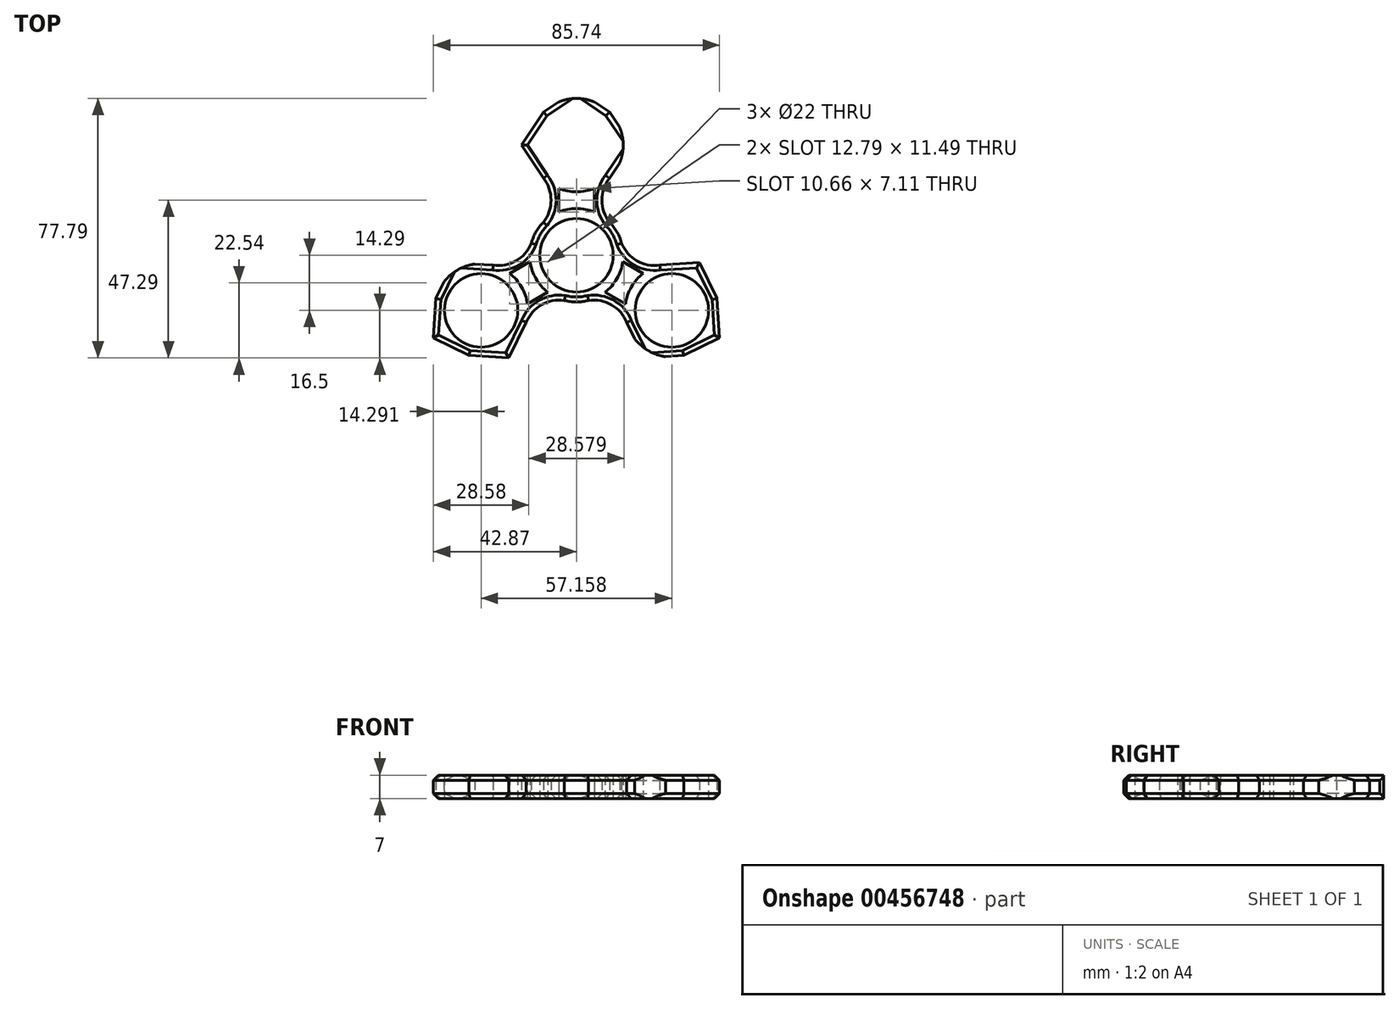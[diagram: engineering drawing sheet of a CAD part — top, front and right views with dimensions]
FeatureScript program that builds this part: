
annotation { "Feature Type Name" : "Feature", "Feature Type Description" : "" }
export const myFeature = defineFeature(function(context is Context, id is Id, definition is map)
    precondition{}
    {
        {
            var Q0;
            Q0=qCreatedBy(makeId("Top.planeOp"),FACE);
            var sketch = newSketch(context, id + "F0", { "sketchPlane" : qUnion([Q0])});
            skCircle(sketch, "E0", {"center": v(0, 0) * mm, "radius": 11 * mm});
            skArc(sketch, "E1.0", {"start": v(-9.9, 9.9) * mm, "mid": v(0, -14) * mm, "end": v(9.9, 9.9) * mm});
            skCircle(sketch, "E2.MirrorC", {"center": v(0, 33) * mm, "radius": 11 * mm});
            skArc(sketch, "E3.MirrorC", {"start": v(5.33, 20.06) * mm, "mid": v(0, 19) * mm, "end": v(-5.33, 20.06) * mm});
            skLineSegment(sketch, "E4.MirrorCS", {"start": v(0, 33) * mm, "end": v(0, 16.5) * mm});
            skLineSegment(sketch, "E5.MirrorCS", {"start": v(-9.9, 23.1) * mm, "end": v(0, 16.5) * mm});
            skLineSegment(sketch, "E6.MirrorCS", {"start": v(0, 16.5) * mm, "end": v(9.9, 23.1) * mm});
            skArc(sketch, "E7.trimOffspring", {"start": v(5.33, 12.94) * mm, "mid": v(0, 14) * mm, "end": v(-5.33, 12.94) * mm});
            skLineSegment(sketch, "E8", {"start": v(5.33, 20.06) * mm, "end": v(5.33, 12.94) * mm});
            skLineSegment(sketch, "E9", {"start": v(-5.33, 12.94) * mm, "end": v(-5.33, 20.06) * mm});
            skLineSegment(sketch, "E10", {"start": v(0, 33) * mm, "end": v(7.48, 33) * mm});
            skLineSegment(sketch, "E11.MirrorCS", {"start": v(0, 49.5) * mm, "end": v(9.9, 42.9) * mm});
            skLineSegment(sketch, "E12.MirrorCS", {"start": v(-9.9, 42.9) * mm, "end": v(0, 49.5) * mm});
            skArc(sketch, "E13.trimOffspring", {"start": v(-5.33, 45.94) * mm, "mid": v(0, 47) * mm, "end": v(5.33, 45.94) * mm});
            skArc(sketch, "E14.trimOffspring", {"start": v(12.94, 38.33) * mm, "mid": v(14, 33) * mm, "end": v(12.94, 27.67) * mm});
            skPoint(sketch, "E15", {"position": v(7.62, 16.5) * mm});
            skArc(sketch, "E16", {"start": v(9.9, 23.1) * mm, "mid": v(7.62, 16.5) * mm, "end": v(9.9, 9.9) * mm});
            skPoint(sketch, "E17.start.orphan", {"position": v(9.9, 16.5) * mm});
            skArc(sketch, "E18.MirrorCS", {"start": v(-9.9, 23.1) * mm, "mid": v(-7.62, 16.5) * mm, "end": v(-9.9, 9.9) * mm});
            skPoint(sketch, "E19.start.orphan", {"position": v(5.33, 16.5) * mm});
            skLineSegment(sketch, "E20.1.0", {"start": v(16.5, 33) * mm, "end": v(9.9, 23.1) * mm});
            skLineSegment(sketch, "E20.1.1", {"start": v(9.9, 42.9) * mm, "end": v(16.5, 33) * mm});
            skLineSegment(sketch, "E20.3.0", {"start": v(-16.5, 33) * mm, "end": v(-9.9, 42.9) * mm});
            skLineSegment(sketch, "E20.3.1", {"start": v(-9.9, 23.1) * mm, "end": v(-16.5, 33) * mm});
            skLineSegment(sketch, "E20.anchor1", {"start": v(0, 33) * mm, "end": v(0, 49.5) * mm, "construction": true});
            skLineSegment(sketch, "E20.anchor2", {"start": v(0, 33) * mm, "end": v(-16.5, 33) * mm, "construction": true});
            skLineSegment(sketch, "E21.1.0", {"start": v(-42.87, -24.75) * mm, "end": v(-42.1, -12.88) * mm});
            skLineSegment(sketch, "E21.1.1", {"start": v(-32.2, -30.02) * mm, "end": v(-42.87, -24.75) * mm});
            skArc(sketch, "E21.1.2", {"start": v(-37.12, -27.6) * mm, "mid": v(-40.7, -23.5) * mm, "end": v(-42.46, -18.35) * mm});
            skLineSegment(sketch, "E21.1.3", {"start": v(-20.33, -30.79) * mm, "end": v(-32.2, -30.02) * mm});
            skCircle(sketch, "E21.1.4", {"center": v(-28.58, -16.5) * mm, "radius": 11 * mm});
            skLineSegment(sketch, "E21.1.5", {"start": v(-15.06, -20.12) * mm, "end": v(-20.33, -30.79) * mm});
            skLineSegment(sketch, "E21.1.6", {"start": v(-15.06, -20.12) * mm, "end": v(-14.29, -8.25) * mm});
            skArc(sketch, "E21.1.7", {"start": v(-20.03, -5.4) * mm, "mid": v(-16.45, -9.5) * mm, "end": v(-14.7, -14.65) * mm});
            skLineSegment(sketch, "E21.1.8", {"start": v(-14.29, -8.25) * mm, "end": v(-24.96, -2.98) * mm});
            skArc(sketch, "E21.1.9", {"start": v(-39.67, -7.96) * mm, "mid": v(-35.58, -4.38) * mm, "end": v(-30.43, -2.62) * mm});
            skLineSegment(sketch, "E21.1.10", {"start": v(-36.83, -2.21) * mm, "end": v(-24.96, -2.98) * mm});
            skLineSegment(sketch, "E21.1.11", {"start": v(-42.1, -12.88) * mm, "end": v(-36.83, -2.21) * mm});
            skArc(sketch, "E21.1.12", {"start": v(-24.96, -2.98) * mm, "mid": v(-18.1, -1.65) * mm, "end": v(-13.52, 3.62) * mm});
            skLineSegment(sketch, "E21.1.13", {"start": v(-20.03, -5.4) * mm, "end": v(-13.88, -1.85) * mm});
            skLineSegment(sketch, "E21.1.14", {"start": v(-8.54, -11.1) * mm, "end": v(-14.7, -14.65) * mm});
            skArc(sketch, "E21.1.15", {"start": v(-15.06, -20.12) * mm, "mid": v(-10.48, -14.85) * mm, "end": v(-3.62, -13.52) * mm});
            skLineSegment(sketch, "E21.2.0", {"start": v(42.87, -24.75) * mm, "end": v(32.2, -30.02) * mm});
            skLineSegment(sketch, "E21.2.1", {"start": v(42.1, -12.88) * mm, "end": v(42.87, -24.75) * mm});
            skArc(sketch, "E21.2.2", {"start": v(42.46, -18.35) * mm, "mid": v(40.7, -23.5) * mm, "end": v(37.12, -27.6) * mm});
            skLineSegment(sketch, "E21.2.3", {"start": v(36.83, -2.21) * mm, "end": v(42.1, -12.88) * mm});
            skCircle(sketch, "E21.2.4", {"center": v(28.58, -16.5) * mm, "radius": 11 * mm});
            skLineSegment(sketch, "E21.2.5", {"start": v(24.96, -2.98) * mm, "end": v(36.83, -2.21) * mm});
            skLineSegment(sketch, "E21.2.6", {"start": v(24.96, -2.98) * mm, "end": v(14.29, -8.25) * mm});
            skArc(sketch, "E21.2.7", {"start": v(14.7, -14.65) * mm, "mid": v(16.45, -9.5) * mm, "end": v(20.03, -5.4) * mm});
            skLineSegment(sketch, "E21.2.8", {"start": v(14.29, -8.25) * mm, "end": v(15.06, -20.12) * mm});
            skArc(sketch, "E21.2.9", {"start": v(26.72, -30.38) * mm, "mid": v(21.58, -28.62) * mm, "end": v(17.49, -25.04) * mm});
            skLineSegment(sketch, "E21.2.10", {"start": v(20.33, -30.79) * mm, "end": v(15.06, -20.12) * mm});
            skLineSegment(sketch, "E21.2.11", {"start": v(32.2, -30.02) * mm, "end": v(20.33, -30.79) * mm});
            skArc(sketch, "E21.2.12", {"start": v(15.06, -20.12) * mm, "mid": v(10.48, -14.85) * mm, "end": v(3.62, -13.52) * mm});
            skLineSegment(sketch, "E21.2.13", {"start": v(14.7, -14.65) * mm, "end": v(8.54, -11.1) * mm});
            skLineSegment(sketch, "E21.2.14", {"start": v(13.88, -1.85) * mm, "end": v(20.03, -5.4) * mm});
            skArc(sketch, "E21.2.15", {"start": v(24.96, -2.98) * mm, "mid": v(18.1, -1.65) * mm, "end": v(13.52, 3.62) * mm});
            skSolve(sketch);
        }
        {
            var Q0;
            Q0=makeQuery(id+"F0.imprint","IMPRINT",FACE,{"disambiguationData":[TD([[makeQuery(id+"F0.imprint","IMPRINT",EDGE,{"derivedFrom":sQuery(id+"F0.wireOp",EDGE,"E0")}),-1.0]])]});
            var Q1;
            Q1=makeQuery(id+"F0.imprint","IMPRINT",FACE,{"disambiguationData":[TD([[makeQuery(id+"F0.imprint","IMPRINT",EDGE,{"derivedFrom":sQuery(id+"F0.wireOp",EDGE,"E2.MirrorC")}),1.0]])]});
            var Q2;
            {var subQ3=sQuery(id+"F0.wireOp",EDGE,"E13.trimOffspring");Q2=makeQuery(id+"F0.imprint","IMPRINT",FACE,{"disambiguationData":[TD([[makeQuery(id+"F0.imprint","IMPRINT",EDGE,{"derivedFrom":subQ3}),1.0]])]});}
            var Q3;
            {var subQ0=sQuery(id+"F0.wireOp",EDGE,"E14.trimOffspring");Q3=makeQuery(id+"F0.imprint","IMPRINT",FACE,{"disambiguationData":[TD([[makeQuery(id+"F0.imprint","IMPRINT",EDGE,{"derivedFrom":subQ0}),1.0]])]});}
            var Q4;
            {var subQ1=sQuery(id+"F0.wireOp",EDGE,"E3.MirrorC");var subQ3=sQuery(id+"F0.wireOp",EDGE,"E4.MirrorCS");var subQ4=makeQuery(id+"F0.imprint","INTERSECT",VERTEX,{"derivedFrom":[subQ1,subQ3]});Q4=makeQuery(id+"F0.imprint","IMPRINT",FACE,{"disambiguationData":[TD([[makeQuery(id+"F0.imprint","IMPRINT",EDGE,{"disambiguationData":[TD([[subQ4,-1.0]])],"derivedFrom":subQ1}),1.0]])]});}
            var Q5;
            {var subQ1=sQuery(id+"F0.wireOp",EDGE,"E3.MirrorC");var subQ3=sQuery(id+"F0.wireOp",EDGE,"E4.MirrorCS");var subQ4=makeQuery(id+"F0.imprint","INTERSECT",VERTEX,{"derivedFrom":[subQ1,subQ3]});Q5=makeQuery(id+"F0.imprint","IMPRINT",FACE,{"disambiguationData":[TD([[makeQuery(id+"F0.imprint","IMPRINT",EDGE,{"disambiguationData":[TD([[subQ4,1.0]])],"derivedFrom":subQ1}),1.0]])]});}
            var Q6;
            {var subQ0=sQuery(id+"F0.wireOp",EDGE,"E21.2.14");Q6=makeQuery(id+"F0.imprint","IMPRINT",FACE,{"disambiguationData":[TD([[makeQuery(id+"F0.imprint","IMPRINT",EDGE,{"derivedFrom":subQ0}),1.0]])]});}
            var Q7;
            {var subQ9=sQuery(id+"F0.wireOp",EDGE,"E21.2.2");Q7=makeQuery(id+"F0.imprint","IMPRINT",FACE,{"disambiguationData":[TD([[makeQuery(id+"F0.imprint","IMPRINT",EDGE,{"derivedFrom":subQ9}),-1.0]])]});}
            var Q8;
            {var subQ3=sQuery(id+"F0.wireOp",EDGE,"E21.2.2");Q8=makeQuery(id+"F0.imprint","IMPRINT",FACE,{"disambiguationData":[TD([[makeQuery(id+"F0.imprint","IMPRINT",EDGE,{"derivedFrom":subQ3}),1.0]])]});}
            var Q9;
            {var subQ0=sQuery(id+"F0.wireOp",EDGE,"E21.2.9");Q9=makeQuery(id+"F0.imprint","IMPRINT",FACE,{"disambiguationData":[TD([[makeQuery(id+"F0.imprint","IMPRINT",EDGE,{"derivedFrom":subQ0}),1.0]])]});}
            var Q10;
            {var subQ3=sQuery(id+"F0.wireOp",EDGE,"E21.2.7");Q10=makeQuery(id+"F0.imprint","IMPRINT",FACE,{"disambiguationData":[TD([[makeQuery(id+"F0.imprint","IMPRINT",EDGE,{"derivedFrom":subQ3}),1.0]])]});}
            var Q11;
            {var subQ0=sQuery(id+"F0.wireOp",EDGE,"E21.2.12");Q11=makeQuery(id+"F0.imprint","IMPRINT",FACE,{"disambiguationData":[TD([[makeQuery(id+"F0.imprint","IMPRINT",EDGE,{"derivedFrom":subQ0}),-1.0]])]});}
            var Q12;
            {var subQ0=sQuery(id+"F0.wireOp",EDGE,"E21.1.14");Q12=makeQuery(id+"F0.imprint","IMPRINT",FACE,{"disambiguationData":[TD([[makeQuery(id+"F0.imprint","IMPRINT",EDGE,{"derivedFrom":subQ0}),1.0]])]});}
            var Q13;
            {var subQ9=sQuery(id+"F0.wireOp",EDGE,"E21.1.2");Q13=makeQuery(id+"F0.imprint","IMPRINT",FACE,{"disambiguationData":[TD([[makeQuery(id+"F0.imprint","IMPRINT",EDGE,{"derivedFrom":subQ9}),-1.0]])]});}
            var Q14;
            {var subQ3=sQuery(id+"F0.wireOp",EDGE,"E21.1.7");Q14=makeQuery(id+"F0.imprint","IMPRINT",FACE,{"disambiguationData":[TD([[makeQuery(id+"F0.imprint","IMPRINT",EDGE,{"derivedFrom":subQ3}),1.0]])]});}
            var Q15;
            {var subQ0=sQuery(id+"F0.wireOp",EDGE,"E21.1.12");Q15=makeQuery(id+"F0.imprint","IMPRINT",FACE,{"disambiguationData":[TD([[makeQuery(id+"F0.imprint","IMPRINT",EDGE,{"derivedFrom":subQ0}),-1.0]])]});}
            var Q16;
            {var subQ0=sQuery(id+"F0.wireOp",EDGE,"E21.1.9");Q16=makeQuery(id+"F0.imprint","IMPRINT",FACE,{"disambiguationData":[TD([[makeQuery(id+"F0.imprint","IMPRINT",EDGE,{"derivedFrom":subQ0}),1.0]])]});}
            var Q17;
            {var subQ3=sQuery(id+"F0.wireOp",EDGE,"E21.1.2");Q17=makeQuery(id+"F0.imprint","IMPRINT",FACE,{"disambiguationData":[TD([[makeQuery(id+"F0.imprint","IMPRINT",EDGE,{"derivedFrom":subQ3}),1.0]])]});}
            extrude(context, id + "F1", {"entities" : qUnion([Q0, Q1, Q2, Q3, Q4, Q5, Q6, Q7, Q8, Q9, Q10, Q11, Q12, Q13, Q14, Q15, Q16, Q17]), "depth" : 7 * mm});
        }
        {
            var Q0;
            Q0=makeQuery(id+"F1.opExtrude","CAP_EDGE",EDGE,{"disambiguationData":[OSD([sQuery(id+"F0.wireOp",EDGE,"E12.MirrorCS")])],"isStart":false});
            var Q1;
            Q1=makeQuery(id+"F1.opExtrude","CAP_EDGE",EDGE,{"disambiguationData":[OSD([sQuery(id+"F0.wireOp",EDGE,"E11.MirrorCS")])],"isStart":false});
            var Q2;
            Q2=makeQuery(id+"F1.opExtrude","CAP_EDGE",EDGE,{"disambiguationData":[OSD([sQuery(id+"F0.wireOp",EDGE,"E20.1.1")])],"isStart":false});
            var Q3;
            Q3=makeQuery(id+"F1.opExtrude","CAP_EDGE",EDGE,{"disambiguationData":[OSD([sQuery(id+"F0.wireOp",EDGE,"E20.1.0")])],"isStart":false});
            var Q4;
            Q4=makeQuery(id+"F1.opExtrude","CAP_EDGE",EDGE,{"disambiguationData":[OSD([sQuery(id+"F0.wireOp",EDGE,"E20.3.1")])],"isStart":false});
            var Q5;
            Q5=makeQuery(id+"F1.opExtrude","CAP_EDGE",EDGE,{"disambiguationData":[OSD([sQuery(id+"F0.wireOp",EDGE,"E20.3.0")])],"isStart":false});
            var Q6;
            Q6=makeQuery(id+"F1.opExtrude","CAP_EDGE",EDGE,{"disambiguationData":[OSD([sQuery(id+"F0.wireOp",EDGE,"E18.MirrorCS")])],"isStart":false});
            var Q7;
            Q7=makeQuery(id+"F1.opExtrude","CAP_EDGE",EDGE,{"disambiguationData":[OSD([sQuery(id+"F0.wireOp",EDGE,"E16")])],"isStart":false});
            var Q8;
            {var subQ0=sQuery(id+"F0.wireOp",EDGE,"E1.0");Q8=makeQuery(id+"F1.opExtrude","CAP_EDGE",EDGE,{"disambiguationData":[OSD([subQ0]),TDD([makeQuery(id+"F0.imprint","IMPRINT",EDGE,{"disambiguationData":[TD([[makeQuery(id+"F0.imprint","INTERSECT",VERTEX,{"derivedFrom":[subQ0,sQuery(id+"F0.wireOp",EDGE,"E16")]}),1.0]])],"derivedFrom":subQ0})])],"isStart":false});}
            var Q9;
            Q9=makeQuery(id+"F1.opExtrude","CAP_EDGE",EDGE,{"disambiguationData":[OSD([sQuery(id+"F0.wireOp",EDGE,"E21.2.15")])],"isStart":false});
            var Q10;
            Q10=makeQuery(id+"F1.opExtrude","CAP_EDGE",EDGE,{"disambiguationData":[OSD([sQuery(id+"F0.wireOp",EDGE,"E21.2.5")])],"isStart":false});
            var Q11;
            Q11=makeQuery(id+"F1.opExtrude","CAP_EDGE",EDGE,{"disambiguationData":[OSD([sQuery(id+"F0.wireOp",EDGE,"E21.2.3")])],"isStart":false});
            var Q12;
            Q12=makeQuery(id+"F1.opExtrude","CAP_EDGE",EDGE,{"disambiguationData":[OSD([sQuery(id+"F0.wireOp",EDGE,"E21.2.1")])],"isStart":false});
            var Q13;
            Q13=makeQuery(id+"F1.opExtrude","CAP_EDGE",EDGE,{"disambiguationData":[OSD([sQuery(id+"F0.wireOp",EDGE,"E21.2.0")])],"isStart":false});
            var Q14;
            Q14=makeQuery(id+"F1.opExtrude","CAP_EDGE",EDGE,{"disambiguationData":[OSD([sQuery(id+"F0.wireOp",EDGE,"E21.2.11")])],"isStart":false});
            var Q15;
            Q15=makeQuery(id+"F1.opExtrude","CAP_EDGE",EDGE,{"disambiguationData":[OSD([sQuery(id+"F0.wireOp",EDGE,"E21.2.10")])],"isStart":false});
            var Q16;
            Q16=makeQuery(id+"F1.opExtrude","CAP_EDGE",EDGE,{"disambiguationData":[OSD([sQuery(id+"F0.wireOp",EDGE,"E21.2.12")])],"isStart":false});
            var Q17;
            {var subQ0=sQuery(id+"F0.wireOp",EDGE,"E1.0");Q17=makeQuery(id+"F1.opExtrude","CAP_EDGE",EDGE,{"disambiguationData":[OSD([subQ0]),TDD([makeQuery(id+"F0.imprint","IMPRINT",EDGE,{"disambiguationData":[TD([[makeQuery(id+"F0.imprint","INTERSECT",VERTEX,{"derivedFrom":[subQ0,sQuery(id+"F0.wireOp",EDGE,"E21.1.15")]}),-1.0]])],"derivedFrom":subQ0})])],"isStart":false});}
            var Q18;
            Q18=makeQuery(id+"F1.opExtrude","CAP_EDGE",EDGE,{"disambiguationData":[OSD([sQuery(id+"F0.wireOp",EDGE,"E21.1.15")])],"isStart":false});
            var Q19;
            Q19=makeQuery(id+"F1.opExtrude","CAP_EDGE",EDGE,{"disambiguationData":[OSD([sQuery(id+"F0.wireOp",EDGE,"E21.1.5")])],"isStart":false});
            var Q20;
            Q20=makeQuery(id+"F1.opExtrude","CAP_EDGE",EDGE,{"disambiguationData":[OSD([sQuery(id+"F0.wireOp",EDGE,"E21.1.3")])],"isStart":false});
            var Q21;
            Q21=makeQuery(id+"F1.opExtrude","CAP_EDGE",EDGE,{"disambiguationData":[OSD([sQuery(id+"F0.wireOp",EDGE,"E21.1.1")])],"isStart":false});
            var Q22;
            Q22=makeQuery(id+"F1.opExtrude","CAP_EDGE",EDGE,{"disambiguationData":[OSD([sQuery(id+"F0.wireOp",EDGE,"E21.1.0")])],"isStart":false});
            var Q23;
            Q23=makeQuery(id+"F1.opExtrude","CAP_EDGE",EDGE,{"disambiguationData":[OSD([sQuery(id+"F0.wireOp",EDGE,"E21.1.11")])],"isStart":false});
            var Q24;
            Q24=makeQuery(id+"F1.opExtrude","CAP_EDGE",EDGE,{"disambiguationData":[OSD([sQuery(id+"F0.wireOp",EDGE,"E21.1.10")])],"isStart":false});
            var Q25;
            Q25=makeQuery(id+"F1.opExtrude","CAP_EDGE",EDGE,{"disambiguationData":[OSD([sQuery(id+"F0.wireOp",EDGE,"E21.1.12")])],"isStart":false});
            var Q26;
            {var subQ0=sQuery(id+"F0.wireOp",EDGE,"E1.0");Q26=makeQuery(id+"F1.opExtrude","CAP_EDGE",EDGE,{"disambiguationData":[OSD([subQ0]),TDD([makeQuery(id+"F0.imprint","IMPRINT",EDGE,{"disambiguationData":[TD([[makeQuery(id+"F0.imprint","INTERSECT",VERTEX,{"derivedFrom":[subQ0,sQuery(id+"F0.wireOp",EDGE,"E18.MirrorCS")]}),-1.0]])],"derivedFrom":subQ0})])],"isStart":false});}
            var Q27;
            {var subQ0=sQuery(id+"F0.wireOp",EDGE,"E1.0");Q27=makeQuery(id+"F1.opExtrude","CAP_EDGE",EDGE,{"disambiguationData":[OSD([subQ0]),TDD([makeQuery(id+"F0.imprint","IMPRINT",EDGE,{"disambiguationData":[TD([[makeQuery(id+"F0.imprint","INTERSECT",VERTEX,{"derivedFrom":[subQ0,sQuery(id+"F0.wireOp",EDGE,"E21.1.15")]}),-1.0]])],"derivedFrom":subQ0})])],"isStart":true});}
            var Q28;
            Q28=makeQuery(id+"F1.opExtrude","CAP_EDGE",EDGE,{"disambiguationData":[OSD([sQuery(id+"F0.wireOp",EDGE,"E21.1.15")])],"isStart":true});
            var Q29;
            Q29=makeQuery(id+"F1.opExtrude","CAP_EDGE",EDGE,{"disambiguationData":[OSD([sQuery(id+"F0.wireOp",EDGE,"E21.1.5")])],"isStart":true});
            var Q30;
            Q30=makeQuery(id+"F1.opExtrude","CAP_EDGE",EDGE,{"disambiguationData":[OSD([sQuery(id+"F0.wireOp",EDGE,"E21.1.3")])],"isStart":true});
            var Q31;
            Q31=makeQuery(id+"F1.opExtrude","CAP_EDGE",EDGE,{"disambiguationData":[OSD([sQuery(id+"F0.wireOp",EDGE,"E21.1.1")])],"isStart":true});
            var Q32;
            Q32=makeQuery(id+"F1.opExtrude","CAP_EDGE",EDGE,{"disambiguationData":[OSD([sQuery(id+"F0.wireOp",EDGE,"E21.1.0")])],"isStart":true});
            var Q33;
            Q33=makeQuery(id+"F1.opExtrude","CAP_EDGE",EDGE,{"disambiguationData":[OSD([sQuery(id+"F0.wireOp",EDGE,"E21.1.11")])],"isStart":true});
            var Q34;
            Q34=makeQuery(id+"F1.opExtrude","CAP_EDGE",EDGE,{"disambiguationData":[OSD([sQuery(id+"F0.wireOp",EDGE,"E21.1.10")])],"isStart":true});
            var Q35;
            Q35=makeQuery(id+"F1.opExtrude","CAP_EDGE",EDGE,{"disambiguationData":[OSD([sQuery(id+"F0.wireOp",EDGE,"E21.1.12")])],"isStart":true});
            var Q36;
            {var subQ0=sQuery(id+"F0.wireOp",EDGE,"E1.0");Q36=makeQuery(id+"F1.opExtrude","CAP_EDGE",EDGE,{"disambiguationData":[OSD([subQ0]),TDD([makeQuery(id+"F0.imprint","IMPRINT",EDGE,{"disambiguationData":[TD([[makeQuery(id+"F0.imprint","INTERSECT",VERTEX,{"derivedFrom":[subQ0,sQuery(id+"F0.wireOp",EDGE,"E18.MirrorCS")]}),-1.0]])],"derivedFrom":subQ0})])],"isStart":true});}
            var Q37;
            Q37=makeQuery(id+"F1.opExtrude","CAP_EDGE",EDGE,{"disambiguationData":[OSD([sQuery(id+"F0.wireOp",EDGE,"E18.MirrorCS")])],"isStart":true});
            var Q38;
            Q38=makeQuery(id+"F1.opExtrude","CAP_EDGE",EDGE,{"disambiguationData":[OSD([sQuery(id+"F0.wireOp",EDGE,"E20.3.1")])],"isStart":true});
            var Q39;
            Q39=makeQuery(id+"F1.opExtrude","CAP_EDGE",EDGE,{"disambiguationData":[OSD([sQuery(id+"F0.wireOp",EDGE,"E20.3.0")])],"isStart":true});
            var Q40;
            Q40=makeQuery(id+"F1.opExtrude","CAP_EDGE",EDGE,{"disambiguationData":[OSD([sQuery(id+"F0.wireOp",EDGE,"E12.MirrorCS")])],"isStart":true});
            var Q41;
            Q41=makeQuery(id+"F1.opExtrude","CAP_EDGE",EDGE,{"disambiguationData":[OSD([sQuery(id+"F0.wireOp",EDGE,"E11.MirrorCS")])],"isStart":true});
            var Q42;
            Q42=makeQuery(id+"F1.opExtrude","CAP_EDGE",EDGE,{"disambiguationData":[OSD([sQuery(id+"F0.wireOp",EDGE,"E20.1.1")])],"isStart":true});
            var Q43;
            Q43=makeQuery(id+"F1.opExtrude","CAP_EDGE",EDGE,{"disambiguationData":[OSD([sQuery(id+"F0.wireOp",EDGE,"E20.1.0")])],"isStart":true});
            var Q44;
            Q44=makeQuery(id+"F1.opExtrude","CAP_EDGE",EDGE,{"disambiguationData":[OSD([sQuery(id+"F0.wireOp",EDGE,"E16")])],"isStart":true});
            var Q45;
            {var subQ0=sQuery(id+"F0.wireOp",EDGE,"E1.0");Q45=makeQuery(id+"F1.opExtrude","CAP_EDGE",EDGE,{"disambiguationData":[OSD([subQ0]),TDD([makeQuery(id+"F0.imprint","IMPRINT",EDGE,{"disambiguationData":[TD([[makeQuery(id+"F0.imprint","INTERSECT",VERTEX,{"derivedFrom":[subQ0,sQuery(id+"F0.wireOp",EDGE,"E16")]}),1.0]])],"derivedFrom":subQ0})])],"isStart":true});}
            var Q46;
            Q46=makeQuery(id+"F1.opExtrude","CAP_EDGE",EDGE,{"disambiguationData":[OSD([sQuery(id+"F0.wireOp",EDGE,"E21.2.15")])],"isStart":true});
            var Q47;
            Q47=makeQuery(id+"F1.opExtrude","CAP_EDGE",EDGE,{"disambiguationData":[OSD([sQuery(id+"F0.wireOp",EDGE,"E21.2.5")])],"isStart":true});
            var Q48;
            Q48=makeQuery(id+"F1.opExtrude","CAP_EDGE",EDGE,{"disambiguationData":[OSD([sQuery(id+"F0.wireOp",EDGE,"E21.2.3")])],"isStart":true});
            var Q49;
            Q49=makeQuery(id+"F1.opExtrude","CAP_EDGE",EDGE,{"disambiguationData":[OSD([sQuery(id+"F0.wireOp",EDGE,"E21.2.1")])],"isStart":true});
            var Q50;
            Q50=makeQuery(id+"F1.opExtrude","CAP_EDGE",EDGE,{"disambiguationData":[OSD([sQuery(id+"F0.wireOp",EDGE,"E21.2.0")])],"isStart":true});
            var Q51;
            Q51=makeQuery(id+"F1.opExtrude","CAP_EDGE",EDGE,{"disambiguationData":[OSD([sQuery(id+"F0.wireOp",EDGE,"E21.2.11")])],"isStart":true});
            var Q52;
            Q52=makeQuery(id+"F1.opExtrude","CAP_EDGE",EDGE,{"disambiguationData":[OSD([sQuery(id+"F0.wireOp",EDGE,"E21.2.10")])],"isStart":true});
            var Q53;
            Q53=makeQuery(id+"F1.opExtrude","CAP_EDGE",EDGE,{"disambiguationData":[OSD([sQuery(id+"F0.wireOp",EDGE,"E21.2.12")])],"isStart":true});
            chamfer(context, id + "F2", {"entities" : qUnion([Q0, Q1, Q2, Q3, Q4, Q5, Q6, Q7, Q8, Q9, Q10, Q11, Q12, Q13, Q14, Q15, Q16, Q17, Q18, Q19, Q20, Q21, Q22, Q23, Q24, Q25, Q26, Q27, Q28, Q29, Q30, Q31, Q32, Q33, Q34, Q35, Q36, Q37, Q38, Q39, Q40, Q41, Q42, Q43, Q44, Q45, Q46, Q47, Q48, Q49, Q50, Q51, Q52, Q53]), "width" : 1.5 * mm, "tangentPropagation" : true});
        }
    });
